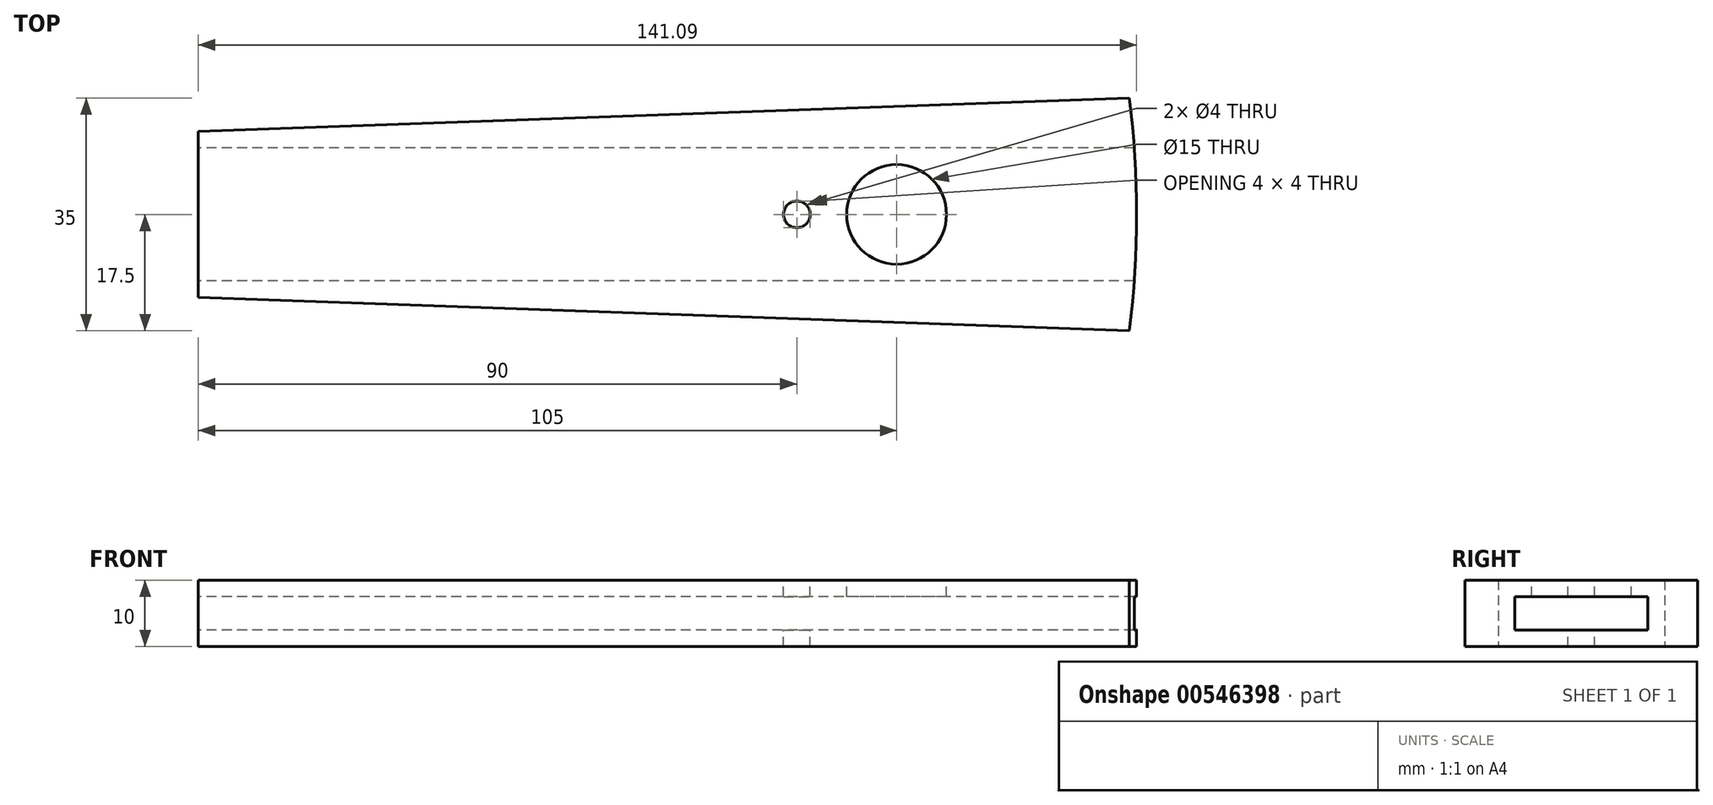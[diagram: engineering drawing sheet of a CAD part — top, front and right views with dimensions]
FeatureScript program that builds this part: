
annotation { "Feature Type Name" : "Feature", "Feature Type Description" : "" }
export const myFeature = defineFeature(function(context is Context, id is Id, definition is map)
    precondition{}
    {
        {
            var Q0;
            Q0=qCreatedBy(makeId("Top.planeOp"),FACE);
            var sketch = newSketch(context, id + "F0", { "sketchPlane" : qUnion([Q0])});
            skPoint(sketch, "E0", {"position": v(-70, 12.5) * mm});
            skPoint(sketch, "E1", {"position": v(-70, -12.5) * mm});
            skPoint(sketch, "E2", {"position": v(70, -17.5) * mm});
            skPoint(sketch, "E3", {"position": v(70, 17.5) * mm});
            skLineSegment(sketch, "E4", {"start": v(-70, 12.5) * mm, "end": v(-70, -12.5) * mm});
            skLineSegment(sketch, "E5", {"start": v(-70, -12.5) * mm, "end": v(70, -17.5) * mm});
            skLineSegment(sketch, "E6", {"start": v(-70, 12.5) * mm, "end": v(70, 17.5) * mm});
            skArc(sketch, "E7", {"start": v(70, -17.5) * mm, "mid": v(71.09, 0) * mm, "end": v(70, 17.5) * mm});
            skCircle(sketch, "E8", {"center": v(35, 0) * mm, "radius": 7.5 * mm});
            skSolve(sketch);
        }
        {
            var Q0;
            Q0=makeQuery(id+"F0.imprint","IMPRINT",FACE,{"disambiguationData":[TD([[makeQuery(id+"F0.imprint","IMPRINT",EDGE,{"derivedFrom":sQuery(id+"F0.wireOp",EDGE,"E4")}),1.0]])]});
            var Q1;
            Q1=makeQuery(id+"F0.imprint","IMPRINT",FACE,{"disambiguationData":[TD([[makeQuery(id+"F0.imprint","IMPRINT",EDGE,{"derivedFrom":sQuery(id+"F0.wireOp",EDGE,"E8")}),1.0]])]});
            extrude(context, id + "F1", {"entities" : qUnion([Q0, Q1]), "depth" : 10 * mm, "offsetDistance" : 25 * mm});
        }
        {
            var Q0;
            Q0=makeQuery(id+"F1.opExtrude","SWEPT_FACE",FACE,{"disambiguationData":[OSD([sQuery(id+"F0.wireOp",EDGE,"E4")])]});
            var sketch = newSketch(context, id + "F2", { "sketchPlane" : qUnion([Q0])});
            skLineSegment(sketch, "E9.bottom", {"start": v(-10, 7.5) * mm, "end": v(10, 7.5) * mm});
            skLineSegment(sketch, "E9.top", {"start": v(-10, 2.5) * mm, "end": v(10, 2.5) * mm});
            skLineSegment(sketch, "E9.left", {"start": v(-10, 7.5) * mm, "end": v(-10, 2.5) * mm});
            skLineSegment(sketch, "E9.right", {"start": v(10, 7.5) * mm, "end": v(10, 2.5) * mm});
            skSolve(sketch);
        }
        {
            var Q0;
            Q0=makeQuery(id+"F2.imprint","IMPRINT",FACE,{"disambiguationData":[TD([[makeQuery(id+"F2.imprint","IMPRINT",EDGE,{"derivedFrom":sQuery(id+"F2.wireOp",EDGE,"E9.bottom")}),-1.0]])]});
            extrude(context, id + "F3", {"entities" : qUnion([Q0]), "operationType" : NewBodyOperationType.REMOVE, "oppositeDirection" : true, "depth" : 200 * mm, "offsetDistance" : 25 * mm});
        }
        {
            var Q0;
            Q0=makeQuery(id+"F1.opExtrude","CAP_FACE",FACE,{"disambiguationData":[OSD([sQuery(id+"F0.wireOp",EDGE,"E4"),sQuery(id+"F0.wireOp",EDGE,"E5"),sQuery(id+"F0.wireOp",EDGE,"E6"),sQuery(id+"F0.wireOp",EDGE,"E7")])],"isStart":false});
            var sketch = newSketch(context, id + "F4", { "sketchPlane" : qUnion([Q0])});
            skCircle(sketch, "E10", {"center": v(35, 0) * mm, "radius": 7.5 * mm});
            skSolve(sketch);
        }
        {
            var Q0;
            Q0=makeQuery(id+"F4.imprint","IMPRINT",FACE,{"disambiguationData":[TD([[makeQuery(id+"F4.imprint","IMPRINT",EDGE,{"derivedFrom":sQuery(id+"F4.wireOp",EDGE,"E10")}),1.0]])]});
            extrude(context, id + "F5", {"entities" : qUnion([Q0]), "operationType" : NewBodyOperationType.REMOVE, "oppositeDirection" : true, "depth" : 2.5 * mm, "offsetDistance" : 25 * mm});
        }
        {
            var Q0;
            Q0=makeQuery(id+"F1.opExtrude","CAP_FACE",FACE,{"disambiguationData":[OSD([sQuery(id+"F0.wireOp",EDGE,"E4"),sQuery(id+"F0.wireOp",EDGE,"E5"),sQuery(id+"F0.wireOp",EDGE,"E6"),sQuery(id+"F0.wireOp",EDGE,"E7")])],"isStart":false});
            var sketch = newSketch(context, id + "F6", { "sketchPlane" : qUnion([Q0])});
            skCircle(sketch, "E11", {"center": v(20, 0) * mm, "radius": 2 * mm});
            skSolve(sketch);
        }
        {
            var Q0;
            Q0=makeQuery(id+"F6.imprint","IMPRINT",FACE,{"disambiguationData":[TD([[makeQuery(id+"F6.imprint","IMPRINT",EDGE,{"derivedFrom":sQuery(id+"F6.wireOp",EDGE,"E11")}),1.0]])]});
            extrude(context, id + "F7", {"entities" : qUnion([Q0]), "operationType" : NewBodyOperationType.REMOVE, "oppositeDirection" : true, "depth" : 10 * mm, "offsetDistance" : 25 * mm});
        }
    });
